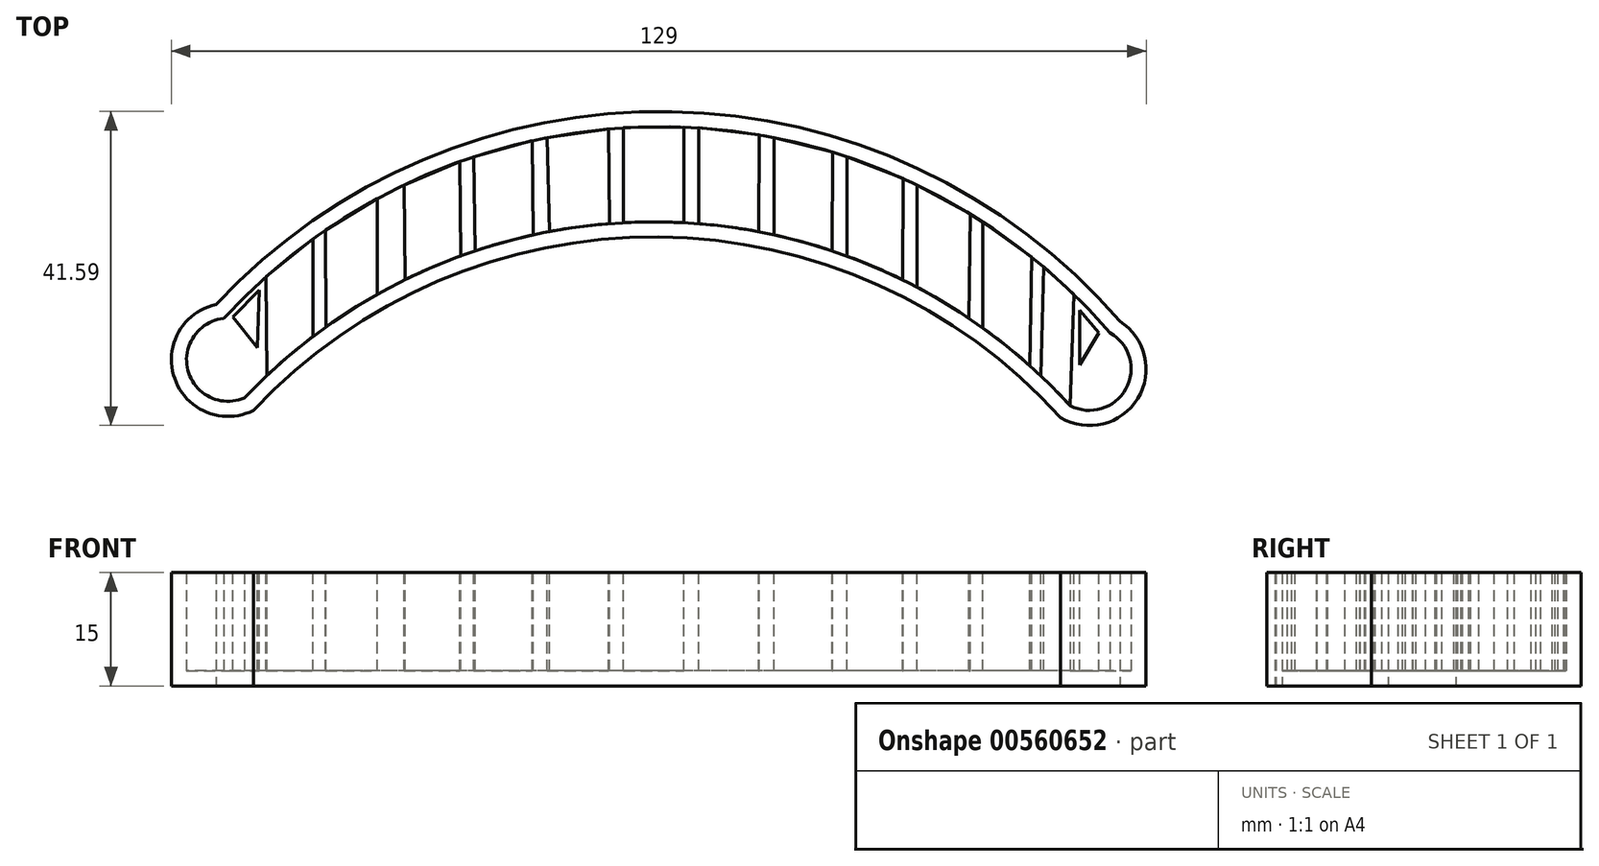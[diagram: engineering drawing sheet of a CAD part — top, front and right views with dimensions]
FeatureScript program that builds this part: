
annotation { "Feature Type Name" : "Feature", "Feature Type Description" : "" }
export const myFeature = defineFeature(function(context is Context, id is Id, definition is map)
    precondition{}
    {
        {
            var Q0;
            Q0=qCreatedBy(makeId("Top.planeOp"),FACE);
            var sketch = newSketch(context, id + "F0", { "sketchPlane" : qUnion([Q0])});
            skArc(sketch, "E0", {"start": v(-100.04, -16.62) * mm, "mid": v(-112.06, -7.98) * mm, "end": v(-103.41, -20) * mm});
            skArc(sketch, "E1", {"start": v(3.43, -20.95) * mm, "mid": v(12.67, -9.31) * mm, "end": v(0.63, -18.02) * mm});
            skArc(sketch, "E2", {"start": v(11.27, -8.16) * mm, "mid": v(-48.05, 19.59) * mm, "end": v(-108.35, -5.96) * mm});
            skArc(sketch, "E3", {"start": v(3.43, -20.95) * mm, "mid": v(-49.79, 2.98) * mm, "end": v(-103.41, -20) * mm});
            skSolve(sketch);
        }
        {
            var Q0;
            Q0 = qSketchRegion(id + "F0", true);
            extrude(context, id + "F1", {"entities" : qUnion([Q0]), "depth" : 15 * mm, "offsetDistance" : 25 * mm});
        }
        {
            var Q0;
            Q0=makeQuery(id+"F1.opExtrude","CAP_FACE",FACE,{"disambiguationData":[OSD([sQuery(id+"F0.wireOp",EDGE,"E0"),sQuery(id+"F0.wireOp",EDGE,"E1"),sQuery(id+"F0.wireOp",EDGE,"E2"),sQuery(id+"F0.wireOp",EDGE,"E3")])],"isStart":false});
            shell(context, id + "F2", {"entities" : qUnion([Q0]), "thickness" : 2 * mm});
        }
        {
            var Q0;
            Q0=makeQuery(id+"F1.opExtrude","CAP_FACE",FACE,{"disambiguationData":[OSD([sQuery(id+"F0.wireOp",EDGE,"E0"),sQuery(id+"F0.wireOp",EDGE,"E1"),sQuery(id+"F0.wireOp",EDGE,"E2"),sQuery(id+"F0.wireOp",EDGE,"E3")])],"isStart":false});
            var sketch = newSketch(context, id + "F3", { "sketchPlane" : qUnion([Q0])});
            skLineSegment(sketch, "E4", {"start": v(-54.43, 17.45) * mm, "end": v(-54.43, 4.87) * mm});
            skLineSegment(sketch, "E5", {"start": v(-54.43, 4.87) * mm, "end": v(-46.43, 4.87) * mm});
            skLineSegment(sketch, "E6", {"start": v(-46.43, 4.87) * mm, "end": v(-46.43, 17.54) * mm});
            skLineSegment(sketch, "E7", {"start": v(-46.43, 17.54) * mm, "end": v(-54.43, 17.45) * mm});
            skLineSegment(sketch, "E8", {"start": v(-54.43, 17.45) * mm, "end": v(-56.43, 17.3) * mm});
            skLineSegment(sketch, "E9", {"start": v(-56.43, 17.3) * mm, "end": v(-56.28, 4.75) * mm});
            skLineSegment(sketch, "E10", {"start": v(-56.28, 4.75) * mm, "end": v(-64.21, 3.7) * mm});
            skLineSegment(sketch, "E11", {"start": v(-56.43, 17.3) * mm, "end": v(-64.54, 16.15) * mm});
            skLineSegment(sketch, "E12", {"start": v(-64.54, 16.15) * mm, "end": v(-64.21, 3.7) * mm});
            skLineSegment(sketch, "E13", {"start": v(-64.54, 16.15) * mm, "end": v(-66.5, 15.74) * mm});
            skLineSegment(sketch, "E14", {"start": v(-66.5, 15.74) * mm, "end": v(-66.36, 3.26) * mm});
            skLineSegment(sketch, "E15", {"start": v(-66.36, 3.26) * mm, "end": v(-74.07, 1.13) * mm});
            skLineSegment(sketch, "E16", {"start": v(-66.5, 15.74) * mm, "end": v(-74.21, 13.62) * mm});
            skLineSegment(sketch, "E17", {"start": v(-74.07, 1.13) * mm, "end": v(-74.21, 13.62) * mm});
            skLineSegment(sketch, "E18", {"start": v(-74.21, 13.62) * mm, "end": v(-76.1, 12.96) * mm});
            skLineSegment(sketch, "E19", {"start": v(-76.1, 12.96) * mm, "end": v(-75.96, 0.47) * mm});
            skLineSegment(sketch, "E20", {"start": v(-75.96, 0.47) * mm, "end": v(-83.32, -2.67) * mm});
            skLineSegment(sketch, "E21", {"start": v(-76.1, 12.96) * mm, "end": v(-83.48, 9.87) * mm});
            skLineSegment(sketch, "E22", {"start": v(-83.32, -2.67) * mm, "end": v(-83.48, 9.87) * mm});
            skLineSegment(sketch, "E23", {"start": v(-83.48, 9.87) * mm, "end": v(-85.28, 8.99) * mm});
            skLineSegment(sketch, "E24", {"start": v(-85.28, 8.99) * mm, "end": v(-85.28, -3.66) * mm});
            skLineSegment(sketch, "E25", {"start": v(-85.28, -3.66) * mm, "end": v(-87.03, -4.62) * mm});
            skLineSegment(sketch, "E26", {"start": v(-87.03, -4.62) * mm, "end": v(-87.03, 8.06) * mm});
            skLineSegment(sketch, "E27", {"start": v(-87.03, 8.06) * mm, "end": v(-93.85, 3.88) * mm});
            skLineSegment(sketch, "E28", {"start": v(-87.03, -4.62) * mm, "end": v(-93.78, -8.92) * mm});
            skLineSegment(sketch, "E29", {"start": v(-93.78, -8.92) * mm, "end": v(-93.85, 3.88) * mm});
            skLineSegment(sketch, "E30", {"start": v(-93.85, 3.88) * mm, "end": v(-95.49, 2.73) * mm});
            skLineSegment(sketch, "E31", {"start": v(-95.49, 2.73) * mm, "end": v(-95.49, -10.17) * mm});
            skLineSegment(sketch, "E32", {"start": v(-95.49, -10.17) * mm, "end": v(-101.6, -15.34) * mm});
            skLineSegment(sketch, "E33", {"start": v(-95.49, 2.73) * mm, "end": v(-101.73, -2.28) * mm});
            skLineSegment(sketch, "E34", {"start": v(-101.73, -2.28) * mm, "end": v(-101.6, -15.34) * mm});
            skLineSegment(sketch, "E35", {"start": v(-102.6, -4.06) * mm, "end": v(-106.1, -7.64) * mm});
            skLineSegment(sketch, "E36", {"start": v(-106.1, -7.64) * mm, "end": v(-102.91, -11.67) * mm});
            skLineSegment(sketch, "E37", {"start": v(-102.91, -11.67) * mm, "end": v(-102.6, -4.06) * mm});
            skLineSegment(sketch, "E38", {"start": v(-46.43, 17.54) * mm, "end": v(-44.44, 17.44) * mm});
            skLineSegment(sketch, "E39", {"start": v(-44.44, 17.44) * mm, "end": v(-44.44, 4.74) * mm});
            skLineSegment(sketch, "E40", {"start": v(-44.44, 4.74) * mm, "end": v(-36.5, 3.67) * mm});
            skLineSegment(sketch, "E41", {"start": v(-44.44, 17.44) * mm, "end": v(-36.49, 16.5) * mm});
            skLineSegment(sketch, "E42", {"start": v(-36.49, 16.5) * mm, "end": v(-36.5, 3.67) * mm});
            skLineSegment(sketch, "E43", {"start": v(-36.49, 16.5) * mm, "end": v(-34.52, 16.15) * mm});
            skLineSegment(sketch, "E44", {"start": v(-34.52, 16.15) * mm, "end": v(-34.52, 3.26) * mm});
            skLineSegment(sketch, "E45", {"start": v(-34.52, 3.26) * mm, "end": v(-26.8, 1.14) * mm});
            skLineSegment(sketch, "E46", {"start": v(-34.52, 16.15) * mm, "end": v(-26.76, 14.22) * mm});
            skLineSegment(sketch, "E47", {"start": v(-26.76, 14.22) * mm, "end": v(-26.8, 1.14) * mm});
            skLineSegment(sketch, "E48", {"start": v(-26.76, 14.22) * mm, "end": v(-24.85, 13.62) * mm});
            skLineSegment(sketch, "E49", {"start": v(-24.85, 13.62) * mm, "end": v(-24.85, 0.46) * mm});
            skLineSegment(sketch, "E50", {"start": v(-24.85, 0.46) * mm, "end": v(-17.5, -2.69) * mm});
            skLineSegment(sketch, "E51", {"start": v(-24.85, 13.62) * mm, "end": v(-17.4, 10.72) * mm});
            skLineSegment(sketch, "E52", {"start": v(-17.4, 10.72) * mm, "end": v(-17.5, -2.69) * mm});
            skLineSegment(sketch, "E53", {"start": v(-17.4, 10.72) * mm, "end": v(-15.58, 9.88) * mm});
            skLineSegment(sketch, "E54", {"start": v(-15.58, 9.88) * mm, "end": v(-15.58, -3.66) * mm});
            skLineSegment(sketch, "E55", {"start": v(-15.58, -3.66) * mm, "end": v(-8.72, -7.78) * mm});
            skLineSegment(sketch, "E56", {"start": v(-15.58, 9.88) * mm, "end": v(-8.56, 6.05) * mm});
            skLineSegment(sketch, "E57", {"start": v(-8.56, 6.05) * mm, "end": v(-8.72, -7.78) * mm});
            skLineSegment(sketch, "E58", {"start": v(-8.56, 6.05) * mm, "end": v(-6.86, 4.98) * mm});
            skLineSegment(sketch, "E59", {"start": v(-6.86, 4.98) * mm, "end": v(-6.86, -9.07) * mm});
            skLineSegment(sketch, "E60", {"start": v(-6.86, -9.07) * mm, "end": v(-0.63, -14.08) * mm});
            skLineSegment(sketch, "E61", {"start": v(-6.86, 4.98) * mm, "end": v(-0.38, 0.3) * mm});
            skLineSegment(sketch, "E62", {"start": v(-0.63, -14.08) * mm, "end": v(-0.38, 0.3) * mm});
            skLineSegment(sketch, "E63", {"start": v(-0.38, 0.3) * mm, "end": v(1.16, -0.98) * mm});
            skLineSegment(sketch, "E64", {"start": v(-0.63, -14.08) * mm, "end": v(0.84, -15.44) * mm});
            skLineSegment(sketch, "E65", {"start": v(0.84, -15.44) * mm, "end": v(1.16, -0.98) * mm});
            skLineSegment(sketch, "E66", {"start": v(1.16, -0.98) * mm, "end": v(5.2, -4.64) * mm});
            skLineSegment(sketch, "E67", {"start": v(0.84, -15.44) * mm, "end": v(4.69, -19.36) * mm});
            skLineSegment(sketch, "E68", {"start": v(4.69, -19.36) * mm, "end": v(5.2, -4.64) * mm});
            skLineSegment(sketch, "E69", {"start": v(5.95, -6.75) * mm, "end": v(5.95, -13.96) * mm});
            skLineSegment(sketch, "E70", {"start": v(5.95, -6.75) * mm, "end": v(8.49, -9.7) * mm});
            skLineSegment(sketch, "E71", {"start": v(8.49, -9.7) * mm, "end": v(5.95, -13.96) * mm});
            skSolve(sketch);
        }
        {
            var Q0;
            {var subQ0=sQuery(id+"F3.wireOp",EDGE,"E31");Q0=makeQuery(id+"F3.imprint","IMPRINT",FACE,{"disambiguationData":[TD([[makeQuery(id+"F3.imprint","IMPRINT",EDGE,{"derivedFrom":subQ0}),-1.0]])]});}
            var Q1;
            {var subQ0=sQuery(id+"F3.wireOp",EDGE,"E26");Q1=makeQuery(id+"F3.imprint","IMPRINT",FACE,{"disambiguationData":[TD([[makeQuery(id+"F3.imprint","IMPRINT",EDGE,{"derivedFrom":subQ0}),1.0]])]});}
            var Q2;
            {var subQ0=sQuery(id+"F3.wireOp",EDGE,"E19");Q2=makeQuery(id+"F3.imprint","IMPRINT",FACE,{"disambiguationData":[TD([[makeQuery(id+"F3.imprint","IMPRINT",EDGE,{"derivedFrom":subQ0}),-1.0]])]});}
            var Q3;
            {var subQ0=sQuery(id+"F3.wireOp",EDGE,"E14");Q3=makeQuery(id+"F3.imprint","IMPRINT",FACE,{"disambiguationData":[TD([[makeQuery(id+"F3.imprint","IMPRINT",EDGE,{"derivedFrom":subQ0}),-1.0]])]});}
            var Q4;
            {var subQ0=sQuery(id+"F3.wireOp",EDGE,"E9");Q4=makeQuery(id+"F3.imprint","IMPRINT",FACE,{"disambiguationData":[TD([[makeQuery(id+"F3.imprint","IMPRINT",EDGE,{"derivedFrom":subQ0}),-1.0]])]});}
            var Q5;
            {var subQ0=sQuery(id+"F3.wireOp",EDGE,"E4");Q5=makeQuery(id+"F3.imprint","IMPRINT",FACE,{"disambiguationData":[TD([[makeQuery(id+"F3.imprint","IMPRINT",EDGE,{"derivedFrom":subQ0}),1.0]])]});}
            var Q6;
            {var subQ0=sQuery(id+"F3.wireOp",EDGE,"E39");Q6=makeQuery(id+"F3.imprint","IMPRINT",FACE,{"disambiguationData":[TD([[makeQuery(id+"F3.imprint","IMPRINT",EDGE,{"derivedFrom":subQ0}),1.0]])]});}
            var Q7;
            {var subQ0=sQuery(id+"F3.wireOp",EDGE,"E44");Q7=makeQuery(id+"F3.imprint","IMPRINT",FACE,{"disambiguationData":[TD([[makeQuery(id+"F3.imprint","IMPRINT",EDGE,{"derivedFrom":subQ0}),1.0]])]});}
            var Q8;
            {var subQ0=sQuery(id+"F3.wireOp",EDGE,"E49");Q8=makeQuery(id+"F3.imprint","IMPRINT",FACE,{"disambiguationData":[TD([[makeQuery(id+"F3.imprint","IMPRINT",EDGE,{"derivedFrom":subQ0}),1.0]])]});}
            var Q9;
            {var subQ0=sQuery(id+"F3.wireOp",EDGE,"E54");Q9=makeQuery(id+"F3.imprint","IMPRINT",FACE,{"disambiguationData":[TD([[makeQuery(id+"F3.imprint","IMPRINT",EDGE,{"derivedFrom":subQ0}),1.0]])]});}
            var Q10;
            {var subQ0=sQuery(id+"F3.wireOp",EDGE,"E59");Q10=makeQuery(id+"F3.imprint","IMPRINT",FACE,{"disambiguationData":[TD([[makeQuery(id+"F3.imprint","IMPRINT",EDGE,{"derivedFrom":subQ0}),1.0]])]});}
            var Q11;
            {var subQ0=sQuery(id+"F3.wireOp",EDGE,"E65");Q11=makeQuery(id+"F3.imprint","IMPRINT",FACE,{"disambiguationData":[TD([[makeQuery(id+"F3.imprint","IMPRINT",EDGE,{"derivedFrom":subQ0}),-1.0]])]});}
            var Q12;
            Q12=makeQuery(id+"F3.imprint","IMPRINT",FACE,{"disambiguationData":[TD([[makeQuery(id+"F3.imprint","IMPRINT",EDGE,{"derivedFrom":sQuery(id+"F3.wireOp",EDGE,"E69")}),1.0]])]});
            var Q13;
            Q13=makeQuery(id+"F3.imprint","IMPRINT",FACE,{"disambiguationData":[TD([[makeQuery(id+"F3.imprint","IMPRINT",EDGE,{"derivedFrom":sQuery(id+"F3.wireOp",EDGE,"E35")}),1.0]])]});
            var Q14;
            Q14=makeQuery(id+"F2.opShell","OFFSET_FACE",FACE,{"disambiguationData":[OSD([sQuery(id+"F0.wireOp",EDGE,"E0"),sQuery(id+"F0.wireOp",EDGE,"E1"),sQuery(id+"F0.wireOp",EDGE,"E2"),sQuery(id+"F0.wireOp",EDGE,"E3")])]});
            extrude(context, id + "F4", {"entities" : qUnion([Q0, Q1, Q2, Q3, Q4, Q5, Q6, Q7, Q8, Q9, Q10, Q11, Q12, Q13]), "endBound" : BoundingType.UP_TO_SURFACE, "oppositeDirection" : true, "depth" : 25 * mm, "endBoundEntityFace" : qUnion([Q14]), "offsetDistance" : 25 * mm});
        }
    });
